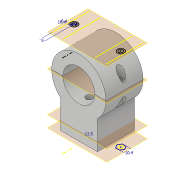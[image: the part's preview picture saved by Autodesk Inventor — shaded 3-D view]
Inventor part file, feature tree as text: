
AUTODESK INVENTOR PART (.ipt)
format: ipt  version: 2021 (Build 250183000, 183)  size: 211,456 bytes
history: native  units: mm
features: other x7, extrude x5, split x2, sketch x2, hole x1, imported_body x1
ambient origin geometry x8: Origin, YZ Plane, XZ Plane, XY Plane, X Axis, Y Axis, Z Axis, Center Point
bodies: Solid1 (feature_tree)
feature tree (18):
  extrude  "Extrusion1"  Depth=85.0mm
  other  "BoltPlane"
  other  "BoltHoles"
  extrude  "Extrusion2"  Depth=62.0mm
  extrude  "Extrusion3"  Depth=62.0mm TaperAngle=0.0deg
  other  "NutPlane"
  other  "NutHoles"
  extrude  "Extrusion4"  Depth=62.0mm
  other  "SplitPlane"
  split  "Split2"
  hole  "Hole2"  [1 undecoded]
  sketch  "Sketch4"  dims[d2=75.866mm d3=29.0mm d4=58.0mm d5=0.0mm d6=50.0mm d7=6.0mm d8=6.4mm d9=10.4mm d10=58.0mm d11=0.0mm d12=40.0mm d13=0.0mm d14=-80.0mm d15=10.4mm d16=70.0mm d17=0.0mm d18=0.0mm d28=12.5mm d29=6.2mm d30=6.0mm d31=4.0mm d32=2.0mm d33=90.0deg d34=8.0mm d35=0.0mm d36=10.2mm d37=10.2mm d38=18.0mm d39=62.0mm d40=0.0mm]
  other  "BoltHeadLevel"
  extrude  "Extrusion5"  Depth=62.0mm
  split  "Split3"
  sketch  "Sketch1"  dims[d0=50.0mm d1=85.0mm]
  other  "UPPER"
  imported_body  "BASE"
note: 1 required parameter value undecoded (feature->parameter linkage not recoverable at this tier; creation-order binding heuristic only, values carry confidence <= 0.55)
